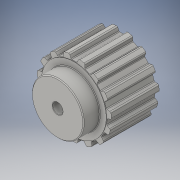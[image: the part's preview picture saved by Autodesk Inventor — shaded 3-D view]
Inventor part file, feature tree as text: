
AUTODESK INVENTOR PART (.ipt)
format: ipt  version: 2016 (Build 200138000, 138)  size: 622,080 bytes
history: native  units: in
note: dims shown in document units (in); Inventor stores cm internally (conversion verified against a paired STEP export)
features: other x4, chamfer x2, direct_edit x1, extrude x1, sketch x1, imported_body x1
ambient origin geometry x8: Origin, YZ Plane, XZ Plane, XY Plane, X Axis, Y Axis, Z Axis, Center Point
bodies: Solid1 (feature_tree)
feature tree (10):
  direct_edit  "Direct Edit1"
  extrude  "Extrusion1"  Depth=1.5748in TaperAngle=0.0deg
  chamfer  "Chamfer1"  Distance=0.0098in Angle=45.0deg
  chamfer  "Chamfer2"  Distance=0.0098in Angle=45.0deg
  sketch  "Sketch1"  dims[d0=0.25in d1=1.5748in d2=0.0in d3=0.0098in d4=0.0787in d5=45.0deg d6=0.0098in d7=0.0787in d8=45.0deg]
  imported_body  "Base1"
  other  "Delete1"
  other  "Delete2"
  other  "Delete3"
  other  "Delete4"
